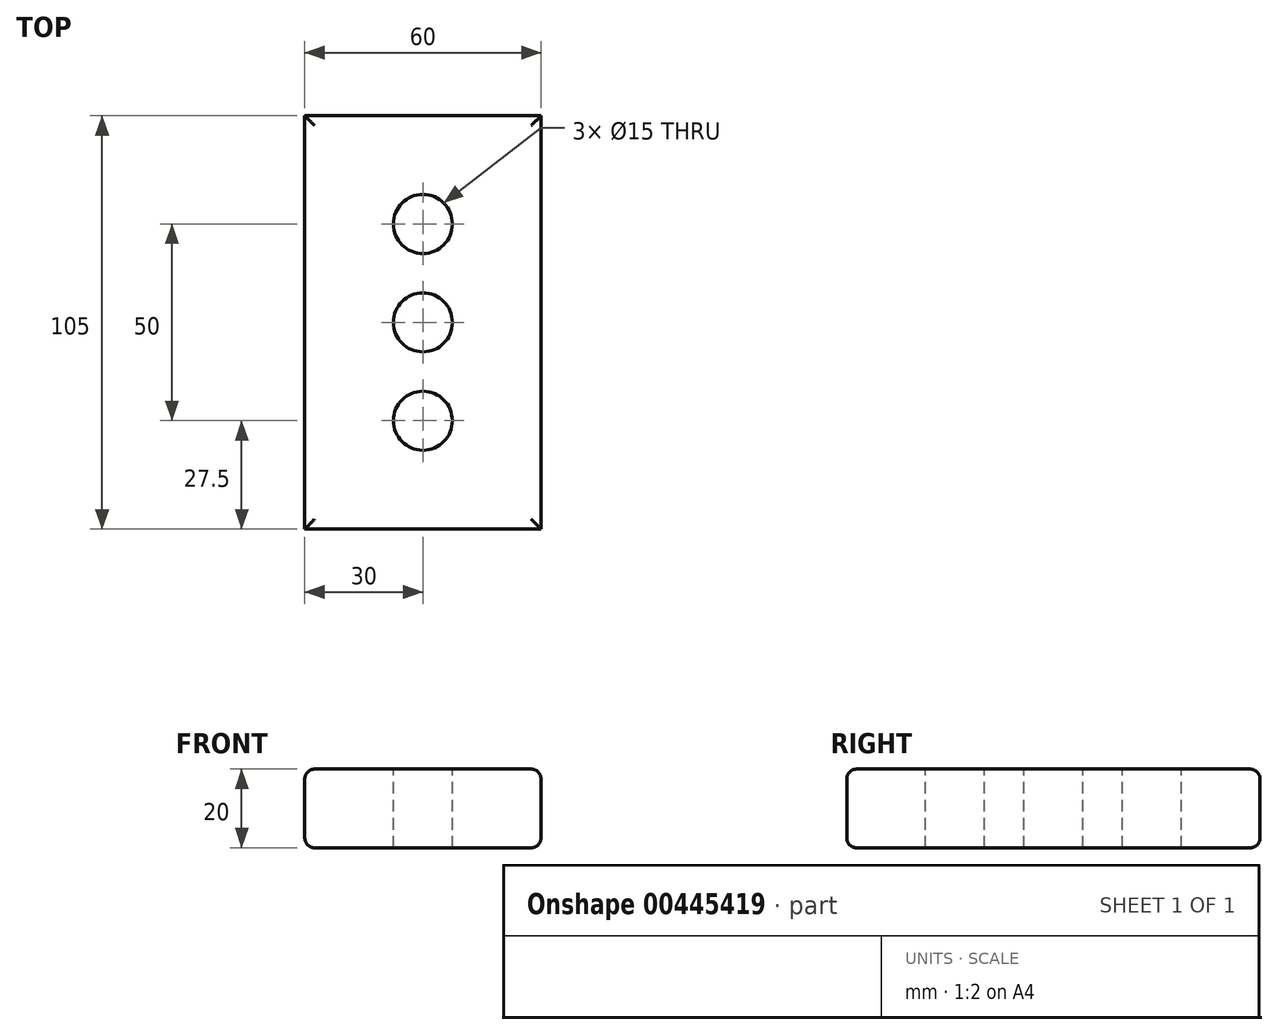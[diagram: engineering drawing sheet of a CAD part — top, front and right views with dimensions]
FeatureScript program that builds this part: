
annotation { "Feature Type Name" : "Feature", "Feature Type Description" : "" }
export const myFeature = defineFeature(function(context is Context, id is Id, definition is map)
    precondition{}
    {
        {
            var Q0;
            Q0=qCreatedBy(makeId("Front.planeOp"),FACE);
            var sketch = newSketch(context, id + "F0", { "sketchPlane" : qUnion([Q0])});
            skLineSegment(sketch, "E0.bottom", {"start": v(30, 10) * mm, "end": v(-30, 10) * mm});
            skLineSegment(sketch, "E0.top", {"start": v(30, -10) * mm, "end": v(-30, -10) * mm});
            skLineSegment(sketch, "E0.left", {"start": v(30, 10) * mm, "end": v(30, -10) * mm});
            skLineSegment(sketch, "E0.right", {"start": v(-30, 10) * mm, "end": v(-30, -10) * mm});
            skPoint(sketch, "E0.middle", {"position": v(0, 0) * mm});
            skSolve(sketch);
        }
        {
            var Q0;
            Q0=makeQuery(id+"F0.imprint","IMPRINT",FACE,{"disambiguationData":[TD([[makeQuery(id+"F0.imprint","IMPRINT",EDGE,{"derivedFrom":sQuery(id+"F0.wireOp",EDGE,"E0.bottom")}),1.0]])]});
            extrude(context, id + "F1", {"entities" : qUnion([Q0]), "endBound" : BoundingType.SYMMETRIC, "depth" : 105 * mm});
        }
        {
            var Q0;
            Q0=makeQuery(id+"F1.opExtrude","SWEPT_FACE",FACE,{"disambiguationData":[OSD([sQuery(id+"F0.wireOp",EDGE,"E0.bottom")])]});
            var sketch = newSketch(context, id + "F2", { "sketchPlane" : qUnion([Q0])});
            skCircle(sketch, "E1", {"center": v(0, 0) * mm, "radius": 7.5 * mm});
            skCircle(sketch, "E2", {"center": v(0, 25) * mm, "radius": 7.5 * mm});
            skCircle(sketch, "E3", {"center": v(0, -25) * mm, "radius": 7.5 * mm});
            skSolve(sketch);
        }
        {
            var Q0;
            Q0=makeQuery(id+"F2.imprint","IMPRINT",FACE,{"disambiguationData":[TD([[makeQuery(id+"F2.imprint","IMPRINT",EDGE,{"derivedFrom":sQuery(id+"F2.wireOp",EDGE,"E2")}),1.0]])]});
            var Q1;
            Q1=makeQuery(id+"F2.imprint","IMPRINT",FACE,{"disambiguationData":[TD([[makeQuery(id+"F2.imprint","IMPRINT",EDGE,{"derivedFrom":sQuery(id+"F2.wireOp",EDGE,"E1")}),1.0]])]});
            var Q2;
            Q2=makeQuery(id+"F2.imprint","IMPRINT",FACE,{"disambiguationData":[TD([[makeQuery(id+"F2.imprint","IMPRINT",EDGE,{"derivedFrom":sQuery(id+"F2.wireOp",EDGE,"E3")}),1.0]])]});
            extrude(context, id + "F3", {"entities" : qUnion([Q0, Q1, Q2]), "operationType" : NewBodyOperationType.REMOVE, "endBound" : BoundingType.THROUGH_ALL, "oppositeDirection" : true, "depth" : 25 * mm});
        }
        {
            var Q0;
            Q0=makeQuery(id+"F1.opExtrude","SWEPT_EDGE",EDGE,{"disambiguationData":[OSD([sQuery(id+"F0.wireOp",EDGE,"E0.bottom"),sQuery(id+"F0.wireOp",EDGE,"E0.right")])]});
            var Q1;
            Q1=makeQuery(id+"F1.opExtrude","CAP_EDGE",EDGE,{"disambiguationData":[OSD([sQuery(id+"F0.wireOp",EDGE,"E0.bottom")])],"isStart":false});
            var Q2;
            Q2=makeQuery(id+"F1.opExtrude","SWEPT_EDGE",EDGE,{"disambiguationData":[OSD([sQuery(id+"F0.wireOp",EDGE,"E0.bottom"),sQuery(id+"F0.wireOp",EDGE,"E0.left")])]});
            var Q3;
            Q3=makeQuery(id+"F1.opExtrude","CAP_EDGE",EDGE,{"disambiguationData":[OSD([sQuery(id+"F0.wireOp",EDGE,"E0.bottom")])],"isStart":true});
            var Q4;
            Q4=makeQuery(id+"F1.opExtrude","CAP_EDGE",EDGE,{"disambiguationData":[OSD([sQuery(id+"F0.wireOp",EDGE,"E0.top")])],"isStart":true});
            var Q5;
            Q5=makeQuery(id+"F1.opExtrude","SWEPT_EDGE",EDGE,{"disambiguationData":[OSD([sQuery(id+"F0.wireOp",EDGE,"E0.top"),sQuery(id+"F0.wireOp",EDGE,"E0.left")])]});
            var Q6;
            Q6=makeQuery(id+"F1.opExtrude","CAP_EDGE",EDGE,{"disambiguationData":[OSD([sQuery(id+"F0.wireOp",EDGE,"E0.top")])],"isStart":false});
            var Q7;
            Q7=makeQuery(id+"F1.opExtrude","SWEPT_EDGE",EDGE,{"disambiguationData":[OSD([sQuery(id+"F0.wireOp",EDGE,"E0.top"),sQuery(id+"F0.wireOp",EDGE,"E0.right")])]});
            fillet(context, id + "F4", {"entities" : qUnion([Q0, Q1, Q2, Q3, Q4, Q5, Q6, Q7]), "radius" : 2.5 * mm, "tangentPropagation" : true, "allowEdgeOverflow" : false});
        }
    });
